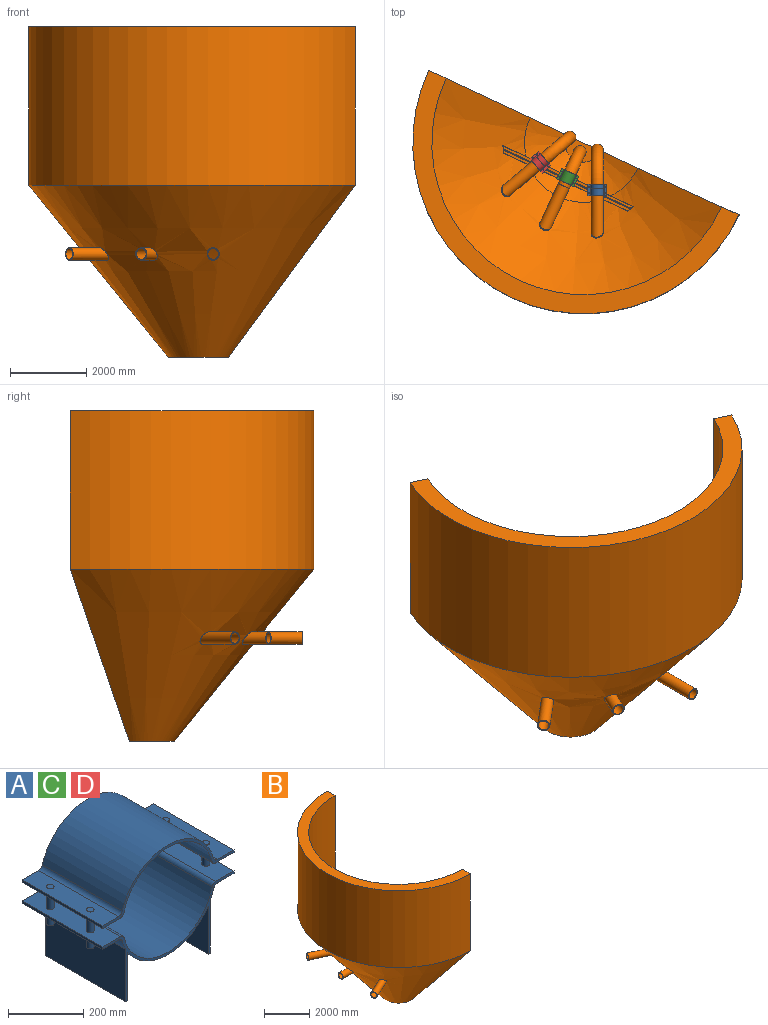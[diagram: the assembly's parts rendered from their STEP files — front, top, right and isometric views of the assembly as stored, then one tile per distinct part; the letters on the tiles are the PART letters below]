
ASSEMBLY  parts=4 mates=6
PART A: 56 faces, bbox 494.7x300x430 mm
  f0: cylinder r=15mm len=300mm, axis (0,1,0), area 5962.9mm2, adj f1,f19,f20,f21
  f1: plane 300x67.89mm, normal (0,0,1), area 19738.2mm2, adj f0,f2,f20,f21,f24,f41
  f2: plane 300x8mm, normal (-1,0,0), area 2400mm2, adj f1,f3,f20,f21
  f3: plane 300x61.75mm, normal (0,0,-1), area 17897.2mm2, adj f2,f4,f20,f21,f23,f44
  f4: cylinder r=15mm len=300mm, axis (0,1,0), area 5816.7mm2, adj f3,f5,f20,f21
  f5: cylinder r=178mm len=300mm, axis (0,1,0), area 10702.1mm2, adj f4,f6,f20,f21
  f6: plane 300x170mm, normal (-1,0,0), area 51000mm2, adj f5,f7,f20,f21
  f7: plane 300x8mm, normal (0,0,-1), area 2400mm2, adj f6,f8,f20,f21
  f8: plane 300x156.14mm, normal (1,0,0), area 46842.7mm2, adj f7,f9,f20,f21
  f9: cylinder r=178mm len=300mm, axis (0,1,0), area 107042.7mm2, adj f8,f10,f20,f21
  f10: plane 300x156.14mm, normal (-1,0,0), area 46842.7mm2, adj f9,f11,f20,f21
  f11: plane 300x8mm, normal (0,0,-1), area 2400mm2, adj f10,f12,f20,f21
  f12: plane 300x170mm, normal (1,0,0), area 51000mm2, adj f11,f13,f20,f21
  f13: cylinder r=178mm len=300mm, axis (0,1,0), area 10702.1mm2, adj f12,f14,f20,f21
  f14: cylinder r=15mm len=300mm, axis (0,1,0), area 5816.7mm2, adj f13,f15,f20,f21
  f15: plane 300x61.75mm, normal (0,0,-1), area 17897.2mm2, adj f14,f16,f20,f21,f49,f54
  f16: plane 300x8mm, normal (1,0,0), area 2400mm2, adj f15,f17,f20,f21
  f17: plane 300x67.89mm, normal (0,0,1), area 19738.2mm2, adj f16,f18,f20,f21,f48,f53
  f18: cylinder r=15mm len=300mm, axis (0,1,0), area 5962.9mm2, adj f17,f19,f20,f21
  f19: cylinder r=170mm len=329.79mm, axis (0,1,0), area 135159mm2, adj f0,f18,f20,f21
  f20: plane 494.66x221.98mm, normal (0,-1,0), area 7653.3mm2, adj f0,f1,f2,f3,f4,f5,f6,f7
  f21: plane 494.66x221.98mm, normal (0,1,0), area 7653.3mm2, adj f0,f1,f2,f3,f4,f5,f6,f7
  f22: plane 20x20mm, normal (0,0,-1), area 314.2mm2, adj f23
  f23: cylinder r=10mm len=44mm, axis (0,0,1), area 2764.6mm2, adj f3,f22
  f24: cylinder r=10mm len=60mm, axis (0,0,1), area 3769.9mm2, adj f1,f35
  f25: cylinder r=170mm len=329.79mm, axis (0,1,0), area 135159mm2, adj f26,f36,f37,f38
  f26: cylinder r=15mm len=300mm, axis (0,1,0), area 5962.9mm2, adj f25,f27,f37,f38
  f27: plane 300x67.89mm, normal (0,0,-1), area 19738.2mm2, adj f26,f28,f37,f38,f48,f53
  f28: plane 300x8mm, normal (1,0,0), area 2400mm2, adj f27,f29,f37,f38
  f29: plane 300x61.75mm, normal (0,0,1), area 17897.2mm2, adj f28,f30,f37,f38,f47,f52
  f30: cylinder r=15mm len=300mm, axis (0,1,0), area 5816.7mm2, adj f29,f31,f37,f38
  f31: cylinder r=178mm len=342.31mm, axis (0,1,0), area 138050.8mm2, adj f30,f32,f37,f38
  f32: cylinder r=15mm len=300mm, axis (0,1,0), area 5816.7mm2, adj f31,f33,f37,f38
  f33: plane 300x61.75mm, normal (0,0,1), area 17897.2mm2, adj f32,f34,f37,f38,f39,f43
  f34: plane 300x8mm, normal (-1,0,0), area 2400mm2, adj f33,f35,f37,f38
  f35: plane 300x67.89mm, normal (0,0,-1), area 19738.2mm2, adj f24,f34,f36,f37,f38,f41
  f36: cylinder r=15mm len=300mm, axis (0,1,0), area 5962.9mm2, adj f25,f35,f37,f38
  f37: plane 494.66x148mm, normal (0,-1,0), area 5048mm2, adj f25,f26,f27,f28,f29,f30,f31,f32
  f38: plane 494.66x148mm, normal (0,1,0), area 5048mm2, adj f25,f26,f27,f28,f29,f30,f31,f32
  f39: cylinder r=10mm len=20mm, axis (0,0,1), area 62.8mm2, adj f33,f40
  f40: plane 20x20mm, normal (0,0,1), area 314.2mm2, adj f39
  f41: cylinder r=10mm len=60mm, axis (0,0,1), area 3769.9mm2, adj f1,f35
  f42: plane 20x20mm, normal (0,0,1), area 314.2mm2, adj f43
  f43: cylinder r=10mm len=20mm, axis (0,0,1), area 62.8mm2, adj f33,f42
  f44: cylinder r=10mm len=44mm, axis (0,0,1), area 2764.6mm2, adj f3,f45
  f45: plane 20x20mm, normal (0,0,-1), area 314.2mm2, adj f44
  f46: plane 20x20mm, normal (0,0,1), area 314.2mm2, adj f47
  f47: cylinder r=10mm len=20mm, axis (0,0,1), area 62.8mm2, adj f29,f46
  f48: cylinder r=10mm len=60mm, axis (0,0,1), area 3769.9mm2, adj f17,f27
  f49: cylinder r=10mm len=44mm, axis (0,0,1), area 2764.6mm2, adj f15,f50
  f50: plane 20x20mm, normal (0,0,-1), area 314.2mm2, adj f49
  f51: plane 20x20mm, normal (0,0,1), area 314.2mm2, adj f52
  f52: cylinder r=10mm len=20mm, axis (0,0,1), area 62.8mm2, adj f29,f51
  f53: cylinder r=10mm len=60mm, axis (0,0,1), area 3769.9mm2, adj f17,f27
  f54: cylinder r=10mm len=44mm, axis (0,0,1), area 2764.6mm2, adj f15,f55
  f55: plane 20x20mm, normal (0,0,-1), area 314.2mm2, adj f54
PART B: 61 faces, bbox 4711.3x9000x8700 mm
  f0: plane 9000x4500mm, normal (0,0,1), area 6675884.4mm2, adj f1,f7,f8
  f1: cylinder r=4500mm len=9000mm, axis (0,0,1), area 59058701.6mm2, adj f0,f2,f8
  f2: cone r=4500mm half-angle=39.1deg, axis (0,0,1), area 48421743.6mm2, adj f1,f3,f8,f34,f46,f58
  f3: plane 1649.51x824.75mm, normal (0,0,-1), area 1068487mm2, adj f2,f8
  f4: plane 1000x500mm, normal (0,0,1), area 392699.1mm2, adj f5,f8
  f5: cone r=500mm half-angle=46.7deg, axis (0,0,1), area 4724745.6mm2, adj f4,f6,f8
  f6: cone r=1562mm half-angle=39.1deg, axis (0,0,1), area 33437078.5mm2, adj f5,f7,f8,f9,f10,f11,f12,f13
  f7: cylinder r=4000mm len=8000mm, axis (0,0,1), area 50265482.5mm2, adj f0,f6,f8
  f8: plane 9000x8700mm, normal (1,0,0), area 10930880.6mm2, adj f0,f1,f2,f3,f4,f5,f6,f7
  f9: plane 3122.68x68.05mm, normal (0,0,1), area 209240.7mm2, adj f6,f17,f18
  f10: plane 3227.09x165mm, normal (0,0,-1), area 514819.5mm2, adj f6,f18,f19
  f11: plane 3246.4x68.05mm, normal (0,0,1), area 218068.3mm2, adj f6,f19,f20
  f12: plane 3778.51x68.05mm, normal (0,0,-1), area 254684.8mm2, adj f6,f22,f23
  f13: plane 3797.12x165mm, normal (0,0,1), area 611622.3mm2, adj f6,f23,f24
  f14: plane 3672.75x68.05mm, normal (0,0,-1), area 247169mm2, adj f6,f15,f24
  f15: cylinder r=11.4mm len=3676.49mm, axis (0,1,0), area 65779.1mm2, adj f6,f14,f16
  f16: plane 3664.54x263.83mm, normal (-1,0,0), area 900659.9mm2, adj f6,f15,f17
  f17: cylinder r=11.4mm len=3160.4mm, axis (0,1,0), area 56239.4mm2, adj f6,f9,f16
  f18: plane 3025.43x10.22mm, normal (-1,0,0), area 30753.5mm2, adj f6,f9,f10
  f19: plane 3246.42x10.21mm, normal (1,0,0), area 33014.8mm2, adj f6,f10,f11
  f20: cylinder r=11.4mm len=3168.49mm, axis (0,1,0), area 56583.2mm2, adj f6,f11,f21
  f21: plane 3671.54x263.84mm, normal (1,0,0), area 902640.8mm2, adj f6,f20,f22
  f22: cylinder r=11.4mm len=3705.66mm, axis (0,1,0), area 66072.8mm2, adj f6,f12,f21
  f23: plane 3797.13x10.21mm, normal (1,0,0), area 38635.7mm2, adj f6,f12,f13
  f24: plane 3610.02x10.21mm, normal (-1,0,0), area 36722.2mm2, adj f6,f13,f14
  f25: cylinder r=161.95mm len=670mm, axis (0,0,-1), area 681766.4mm2, adj f26,f28
  f26: torus R=1000mm, axis (0,1,0), area 1598382.4mm2, adj f25,f27
  f27: cylinder r=161.95mm len=1272.54mm, axis (1,0,0), area 1158144.4mm2, adj f6,f26
  f28: plane 323.9x323.9mm, normal (0,0,-1), area 19094.6mm2, adj f25,f29
  f29: cylinder r=141.95mm len=670mm, axis (0,0,-1), area 597571.8mm2, adj f28,f30
  f30: torus R=1000mm, axis (0,1,0), area 1400990.3mm2, adj f29,f31
  f31: cylinder r=141.95mm len=1256.28mm, axis (1,0,0), area 1015720.6mm2, adj f30,f32
  f32: cone r=1562mm half-angle=39.1deg, axis (0,0,1), area 81599.5mm2, adj f31
  f33: cylinder r=141.95mm len=730.15mm, axis (1,0,0), area 549829.5mm2, adj f35,f36
  f34: cylinder r=161.95mm len=746.41mm, axis (1,0,0), area 627709.6mm2, adj f2,f35
  f35: plane 323.9x323.9mm, normal (-1,0,0), area 19094.6mm2, adj f33,f34
  f36: cone r=4500mm half-angle=39.1deg, axis (0,0,1), area 81588mm2, adj f33
  f37: cylinder r=161.95mm len=670mm, axis (0,0,-1), area 681766.4mm2, adj f38,f40
  f38: torus R=1000mm, axis (-0.42,0.91,0), area 1598382.4mm2, adj f37,f39
  f39: cylinder r=161.95mm len=1323.59mm, axis (0.91,0.42,0), area 1192325mm2, adj f6,f38
  f40: plane 323.9x323.9mm, normal (0,0,-1), area 19094.6mm2, adj f37,f41
  f41: cylinder r=141.95mm len=670mm, axis (0,0,-1), area 597571.8mm2, adj f40,f42
  f42: torus R=1000mm, axis (-0.42,0.91,0), area 1400990.3mm2, adj f41,f43
  f43: cylinder r=141.95mm len=1291.64mm, axis (0.91,0.42,0), area 1045696.1mm2, adj f42,f44
  f44: cone r=1562mm half-angle=39.1deg, axis (0,0,1), area 82507.4mm2, adj f43
  f45: cylinder r=141.95mm len=1291.91mm, axis (0.91,0.42,0), area 1049999.6mm2, adj f47,f48
  f46: cylinder r=161.95mm len=1323.85mm, axis (0.91,0.42,0), area 1198533.4mm2, adj f2,f47
  f47: plane 323.9x293.55mm, normal (-0.91,-0.42,0), area 19094.6mm2, adj f45,f46
  f48: cone r=4500mm half-angle=39.1deg, axis (0,0,1), area 82165.7mm2, adj f45
  f49: cylinder r=161.95mm len=670mm, axis (0,0,-1), area 681766.4mm2, adj f50,f52
  f50: torus R=1000mm, axis (0.42,0.91,0), area 1598382.4mm2, adj f49,f51
  f51: cylinder r=161.95mm len=1323.59mm, axis (0.91,-0.42,0), area 1192323.2mm2, adj f6,f50
  f52: plane 323.9x323.9mm, normal (0,0,-1), area 19094.6mm2, adj f49,f53
  f53: cylinder r=141.95mm len=670mm, axis (0,0,-1), area 597571.8mm2, adj f52,f54
  f54: torus R=1000mm, axis (0.42,0.91,0), area 1400990.3mm2, adj f53,f55
  f55: cylinder r=141.95mm len=1291.64mm, axis (0.91,-0.42,0), area 1045667.5mm2, adj f54,f56
  f56: cone r=1562mm half-angle=39.1deg, axis (0,0,1), area 82495.6mm2, adj f55
  f57: cylinder r=141.95mm len=1291.91mm, axis (0.91,-0.42,0), area 1050010.6mm2, adj f59,f60
  f58: cylinder r=161.95mm len=1323.85mm, axis (0.91,-0.42,0), area 1198499.5mm2, adj f2,f59
  f59: plane 323.9x293.55mm, normal (-0.91,0.42,0), area 19094.6mm2, adj f57,f58
  f60: cone r=4500mm half-angle=39.1deg, axis (0,0,1), area 82146.8mm2, adj f57
PART C: same geometry as A
PART D: same geometry as A
PLACE A t=(-2583.9,-1489.11,-767.76)mm
PLACE B rot(axis=(0,0,1),65deg) t=(-2933.9,-256.3,5058.74)mm fixed
PLACE C rot(axis=(0,0,-1),25deg) t=(-3358.05,-1165.91,-767.76)mm
PLACE D rot(axis=(0,0,-1),50deg) t=(-4079.74,-760.89,-767.76)mm
MATE parallel B.f13 <-> C.f7  axis (0,0,1) through (-3377.35,-1207.29,-1087.76)mm
MATE cylindrical D.f31 <-> B.f51  axis (0.77,0.64,0) through (-4194.65,-857.31,-767.76)mm
MATE cylindrical C.f31 <-> B.f27  axis (0.42,0.91,0) through (-3421.45,-1301.86,-767.76)mm
MATE cylindrical B.f39 <-> A.f31  axis (0,1,0) through (-2583.9,-2105.69,-767.76)mm
MATE parallel B.f13 <-> D.f7  axis (0,0,1) through (-3377.35,-1207.29,-1087.76)mm
MATE parallel A.f11 <-> B.f13  axis (0,0,-1) through (-2429.9,-1489.11,-1019.73)mm
